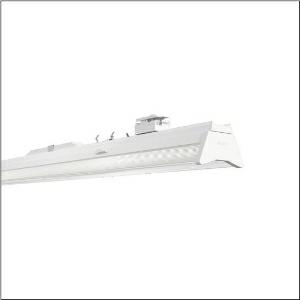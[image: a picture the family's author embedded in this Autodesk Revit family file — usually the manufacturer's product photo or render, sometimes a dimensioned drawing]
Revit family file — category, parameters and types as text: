
# Revit family: licross_r__11_performance_ho_51tm16dn4fxm_a8d0
name_source: partatom
category: Lighting Fixtures
units: mm (PartAtom-declared; Revit-internal decimal feet)

## family parameters
Cut with Voids When Loaded = No
Host = Face
Light Source = No
Part Type = Normal
Room Calculation Point = No
Round Connector Dimension = Use Diameter
Shared = No

## types (1)
- --- (1 x LED, 15460 lm, 87.3 W, 4000K)
    Apparent Load = 87 VA
    CIE Flux Codes = 63 87 95 78 100
    Color Rendering = 80
    Color Temperature = 4000K
    Default Elevation = 1800 mm
    Description = Licross® 11 Performance HO, luminaire insert, of sheet steel, galvanised, coil coated, white, length: 1.500mm, width: 120mm, height: 123mm, LED rated luminous flux: 15.460lm, light colour: 840, control gear: DALI 2, with plug, 5-pole, with phase selection, mains connection: 220..240V, AC, 50/60Hz, rated input power: 87W, internal wiring halogen-free, primary light control with lens, of plastic, primary optical cover: cover, of PMMA, light emission: direct/indirect distribution, primary light characteristic: symmetric, protection rating (complete): IP40, insulation class (complete): insulation class I (protective earthing), certification: CE, ENEC, VDE, UKCA, protection symbol: D if used in an environment without relevant dust loads with corresponding accessories, impact resistance: IK06, permissible ambient temperature for indoor applications: -25..+30°C, corresponds to IFS (International Featured Standards) requirements for safety and quality in the food industry, reducing of maximum allowable ambient temperature of 5°C with ceiling mounting, LABS conformity tested according to VDMA 24364:2018-05, packaging unit: 1 piece
    Height = 114 mm
    Lamp = 1 x LED
    Lamp Light Flux = 15460 lm
    Lamp Power = 87.3 W
    Lamp count = 1
    Length = 1500 mm
    Luminous efficacy = 177 lm/W
    Manufacturer = Siteco
    ModVariant = No
    Model = 51TM16DN4FXM
    Mounting Place = Ceiling
    Mounting Type = Pendant
    Number of Poles = 1
    OnlyDefault = Yes
    Power Factor = 1
    Product Name = Licross® 11 Performance HO
    Product group = luminaire insert | ceiling pendant
    ProductGroupID = 902
    Protection Class = Protection class I
    Protection Degree = IP 40
    RLX_Detail_Level = 1
    RLX_Emergency_Light_Flux = 0 lm
    RLX_Emergency_Type = 0
    RLX_Emergency_Type_DB = No
    RlxData = <blob elided: 34053 chars, md5=097b43cc>
    Socket = socket
    Standby Power = 0 W
    System Light Flux = 15460 lm
    System Power = 87 W
    Type Comments = factory setting: luminous flux: 100 % | dim-lin: 254 | 589 mA
    Type Image = l_1256138.jpg
    URL = http://relux.com
    VarID = @adj_122827
    Voltage = 0 V
    Weight = 0.00 kg
    Width = 120 mm

## geometry (parser evidence)
native form markers: Blend x4, Sweep x11
no freeform markers — native parametric forms only
